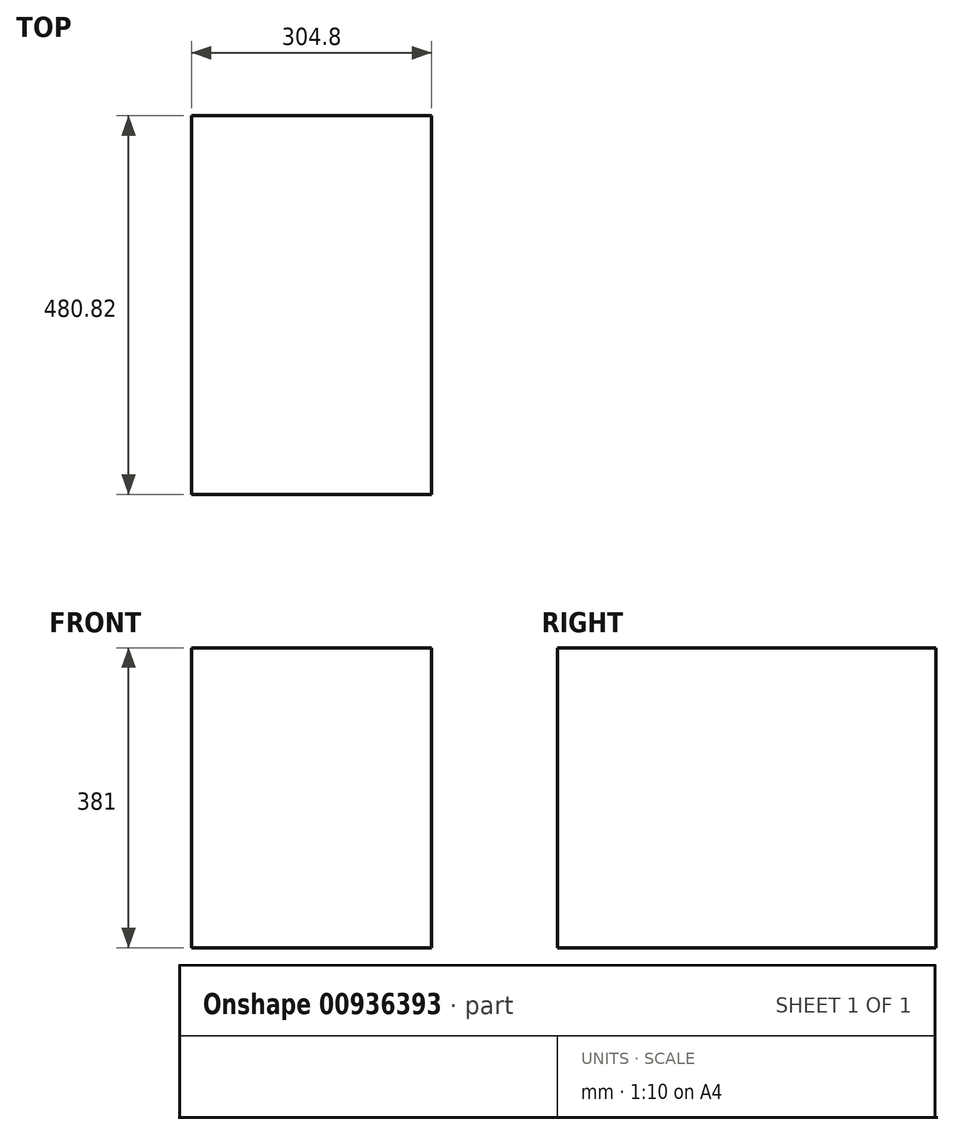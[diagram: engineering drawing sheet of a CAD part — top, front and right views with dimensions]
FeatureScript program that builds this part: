
annotation { "Feature Type Name" : "Feature", "Feature Type Description" : "" }
export const myFeature = defineFeature(function(context is Context, id is Id, definition is map)
    precondition{}
    {
        {
            var Q0;
            Q0=qCreatedBy(makeId("Front.planeOp"),FACE);
            var sketch = newSketch(context, id + "F0", { "sketchPlane" : qUnion([Q0])});
            skLineSegment(sketch, "E0.bottom", {"start": v(0, 0) * mm, "end": v(304.8, 0) * mm});
            skLineSegment(sketch, "E0.top", {"start": v(0, 381) * mm, "end": v(304.8, 381) * mm});
            skLineSegment(sketch, "E0.left", {"start": v(0, 0) * mm, "end": v(0, 381) * mm});
            skLineSegment(sketch, "E0.right", {"start": v(304.8, 0) * mm, "end": v(304.8, 381) * mm});
            skSolve(sketch);
        }
        {
            var Q0;
            Q0=makeQuery(id+"F0.imprint","IMPRINT",FACE,{"disambiguationData":[TD([[makeQuery(id+"F0.imprint","IMPRINT",EDGE,{"derivedFrom":sQuery(id+"F0.wireOp",EDGE,"E0.bottom")}),1.0]])]});
            extrude(context, id + "F1", {"entities" : qUnion([Q0]), "depth" : 480.82 * mm, "offsetDistance" : 25.4 * mm});
        }
    });
